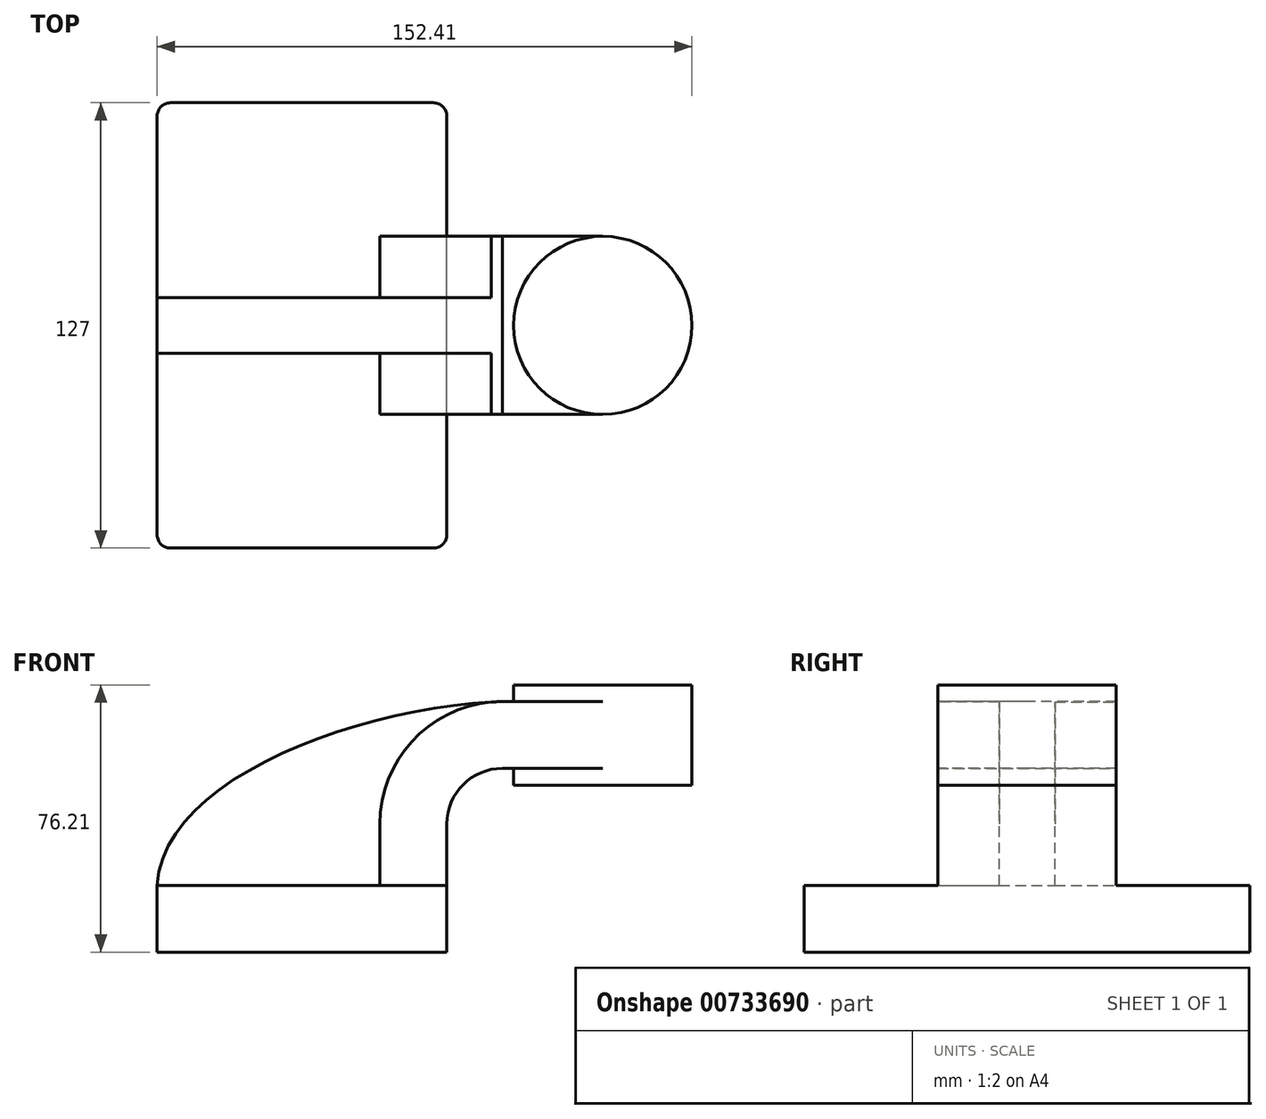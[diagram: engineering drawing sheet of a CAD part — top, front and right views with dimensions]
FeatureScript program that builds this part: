
annotation { "Feature Type Name" : "Feature", "Feature Type Description" : "" }
export const myFeature = defineFeature(function(context is Context, id is Id, definition is map)
    precondition{}
    {
        {
            var Q0;
            Q0=qCreatedBy(makeId("Front.planeOp"),FACE);
            var sketch = newSketch(context, id + "F0", { "sketchPlane" : qUnion([Q0])});
            skLineSegment(sketch, "E0.rect.bottom", {"start": v(-41.28, 9.52) * mm, "end": v(41.28, 9.52) * mm});
            skLineSegment(sketch, "E0.rect.top", {"start": v(-41.28, -9.52) * mm, "end": v(41.28, -9.52) * mm});
            skLineSegment(sketch, "E0.rect.left", {"start": v(-41.28, 9.52) * mm, "end": v(-41.28, -9.52) * mm});
            skLineSegment(sketch, "E0.rect.right", {"start": v(41.28, 9.52) * mm, "end": v(41.28, -9.52) * mm});
            skPoint(sketch, "E0.rect.middle", {"position": v(0, 0) * mm});
            skLineSegment(sketch, "E1", {"start": v(41.28, 9.52) * mm, "end": v(41.28, 27) * mm});
            skArc(sketch, "E2", {"start": v(41.28, 27) * mm, "mid": v(45.92, 38.23) * mm, "end": v(57.15, 42.88) * mm});
            skLineSegment(sketch, "E3", {"start": v(57.15, 42.88) * mm, "end": v(85.72, 42.88) * mm});
            skLineSegment(sketch, "E4.rect.bottom", {"start": v(60.32, 38.1) * mm, "end": v(111.12, 38.1) * mm});
            skLineSegment(sketch, "E4.rect.top", {"start": v(60.32, 66.68) * mm, "end": v(111.12, 66.68) * mm});
            skLineSegment(sketch, "E4.rect.left", {"start": v(60.32, 38.1) * mm, "end": v(60.32, 66.68) * mm});
            skLineSegment(sketch, "E4.rect.right", {"start": v(111.13, 38.1) * mm, "end": v(111.12, 66.68) * mm});
            skPoint(sketch, "E4.rect.middle", {"position": v(85.72, 52.39) * mm});
            skLineSegment(sketch, "E5.0", {"start": v(57.15, 61.93) * mm, "end": v(85.72, 61.93) * mm});
            skArc(sketch, "E5.1", {"start": v(22.23, 27) * mm, "mid": v(32.45, 51.7) * mm, "end": v(57.15, 61.93) * mm});
            skLineSegment(sketch, "E5.2", {"start": v(22.23, 9.52) * mm, "end": v(22.23, 27) * mm});
            skLineSegment(sketch, "E6", {"start": v(85.72, 38.1) * mm, "end": v(85.72, 66.68) * mm});
            skFitSpline(sketch, "E7", {"points": [v(-41.28, 9.53) * mm, v(57.15, 61.93) * mm], "startDerivative": vector(5.2, 92.34) * mm, "endDerivative": vector(120.92, 4.22) * mm});
            skSolve(sketch);
        }
        {
            var Q0;
            Q0=makeQuery(id+"F0.imprint","IMPRINT",FACE,{"disambiguationData":[TD([[makeQuery(id+"F0.imprint","IMPRINT",EDGE,{"derivedFrom":sQuery(id+"F0.wireOp",EDGE,"E0.rect.top")}),1.0]])]});
            extrude(context, id + "F1", {"entities" : qUnion([Q0]), "endBound" : BoundingType.SYMMETRIC, "depth" : 127 * mm, "offsetDistance" : 25.4 * mm});
        }
        {
            var Q0;
            {var subQ4=sQuery(id+"F0.wireOp",EDGE,"E1");Q0=makeQuery(id+"F0.imprint","IMPRINT",FACE,{"disambiguationData":[TD([[makeQuery(id+"F0.imprint","IMPRINT",EDGE,{"derivedFrom":subQ4}),1.0]])]});}
            var Q1;
            {var subQ0=sQuery(id+"F0.wireOp",EDGE,"E6");var subQ1=sQuery(id+"F0.wireOp",EDGE,"E3");var subQ2=makeQuery(id+"F0.imprint","INTERSECT",VERTEX,{"derivedFrom":[subQ1,subQ0]});Q1=makeQuery(id+"F0.imprint","IMPRINT",FACE,{"disambiguationData":[TD([[makeQuery(id+"F0.imprint","IMPRINT",EDGE,{"disambiguationData":[TD([[subQ2,1.0]])],"derivedFrom":subQ1}),1.0]])]});}
            extrude(context, id + "F2", {"entities" : qUnion([Q0, Q1]), "operationType" : NewBodyOperationType.ADD, "endBound" : BoundingType.SYMMETRIC, "depth" : 50.8 * mm, "offsetDistance" : 25.4 * mm});
        }
        {
            var Q0;
            {var subQ3=sQuery(id+"F0.wireOp",EDGE,"E5.2");Q0=makeQuery(id+"F0.imprint","IMPRINT",FACE,{"disambiguationData":[TD([[makeQuery(id+"F0.imprint","IMPRINT",EDGE,{"derivedFrom":subQ3}),1.0]])]});}
            extrude(context, id + "F3", {"entities" : qUnion([Q0]), "operationType" : NewBodyOperationType.ADD, "endBound" : BoundingType.SYMMETRIC, "depth" : 15.88 * mm, "offsetDistance" : 25.4 * mm});
        }
        {
            var Q0;
            {var subQ0=sQuery(id+"F0.wireOp",EDGE,"E4.rect.right");Q0=makeQuery(id+"F0.imprint","IMPRINT",FACE,{"disambiguationData":[TD([[makeQuery(id+"F0.imprint","IMPRINT",EDGE,{"derivedFrom":subQ0}),1.0]])]});}
            var Q1;
            Q1=sQuery(id+"F0.wireOp",EDGE,"E6");
            revolve(context, id + "F4", {"operationType" : NewBodyOperationType.ADD, "surfaceOperationType" : NewSurfaceOperationType.NEW, "entities" : qUnion([Q0]), "axis" : qUnion([Q1]), "revolveType" : RevolveType.FULL});
        }
        {
            var Q0;
            Q0=makeQuery(id+"F1.opExtrude","CAP_EDGE",EDGE,{"disambiguationData":[OSD([sQuery(id+"F0.wireOp",EDGE,"E0.rect.left")])],"isStart":false});
            var Q1;
            Q1=makeQuery(id+"F1.opExtrude","CAP_EDGE",EDGE,{"disambiguationData":[OSD([sQuery(id+"F0.wireOp",EDGE,"E0.rect.right")])],"isStart":false});
            var Q2;
            Q2=makeQuery(id+"F1.opExtrude","CAP_EDGE",EDGE,{"disambiguationData":[OSD([sQuery(id+"F0.wireOp",EDGE,"E0.rect.right")])],"isStart":true});
            var Q3;
            Q3=makeQuery(id+"F1.opExtrude","CAP_EDGE",EDGE,{"disambiguationData":[OSD([sQuery(id+"F0.wireOp",EDGE,"E0.rect.left")])],"isStart":true});
            fillet(context, id + "F5", {"entities" : qUnion([Q0, Q1, Q2, Q3]), "radius" : 3.8 * mm, "tangentPropagation" : true, "allowEdgeOverflow" : false});
        }
    });
